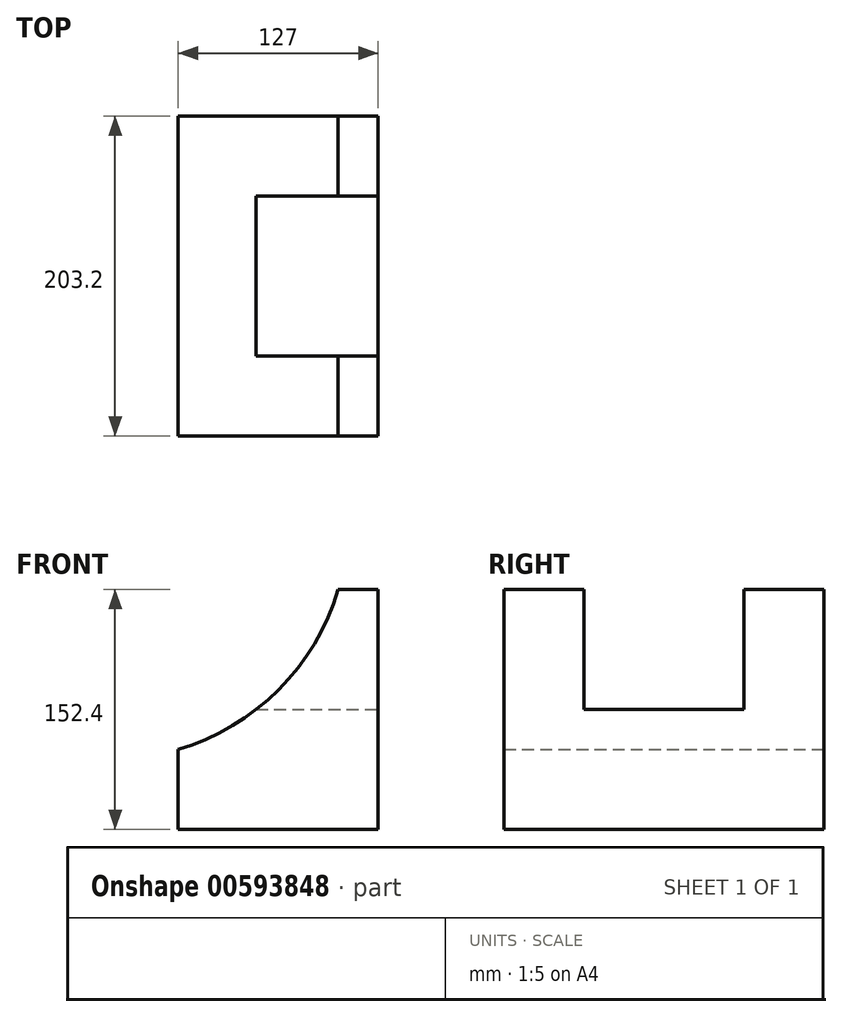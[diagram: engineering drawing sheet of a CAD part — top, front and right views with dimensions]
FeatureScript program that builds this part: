
annotation { "Feature Type Name" : "Feature", "Feature Type Description" : "" }
export const myFeature = defineFeature(function(context is Context, id is Id, definition is map)
    precondition{}
    {
        {
            var Q0;
            Q0=qCreatedBy(makeId("Front.planeOp"),FACE);
            var sketch = newSketch(context, id + "F0", { "sketchPlane" : qUnion([Q0])});
            skLineSegment(sketch, "E0", {"start": v(0, 0) * mm, "end": v(127, 0) * mm});
            skLineSegment(sketch, "E1", {"start": v(127, 0) * mm, "end": v(127, 152.4) * mm});
            skLineSegment(sketch, "E2", {"start": v(127, 152.4) * mm, "end": v(101.6, 152.4) * mm});
            skLineSegment(sketch, "E3", {"start": v(0, 0) * mm, "end": v(0, 50.8) * mm});
            skArc(sketch, "E4", {"start": v(0, 50.8) * mm, "mid": v(63.7, 88.7) * mm, "end": v(101.6, 152.4) * mm});
            skSolve(sketch);
        }
        {
            var Q0;
            Q0 = qSketchRegion(id + "F0", true);
            extrude(context, id + "F1", {"entities" : qUnion([Q0]), "endBound" : BoundingType.SYMMETRIC, "depth" : 203.2 * mm, "offsetDistance" : 25.4 * mm});
        }
        {
            var Q0;
            Q0=makeQuery(id+"F1.opExtrude","SWEPT_FACE",FACE,{"disambiguationData":[OSD([sQuery(id+"F0.wireOp",EDGE,"E1")])]});
            var sketch = newSketch(context, id + "F2", { "sketchPlane" : qUnion([Q0])});
            skLineSegment(sketch, "E5.0", {"start": v(-101.6, 152.4) * mm, "end": v(101.6, 152.4) * mm});
            skPoint(sketch, "E6.0", {"position": v(-101.6, 76.2) * mm});
            skLineSegment(sketch, "E7.0", {"start": v(-101.6, 0) * mm, "end": v(101.6, 0) * mm});
            skLineSegment(sketch, "E8.0", {"start": v(101.6, 0) * mm, "end": v(101.6, 152.4) * mm});
            skLineSegment(sketch, "E9.0.1", {"start": v(101.6, 152.4) * mm, "end": v(-101.6, 152.4) * mm});
            skLineSegment(sketch, "E9.0.2", {"start": v(-101.6, 152.4) * mm, "end": v(-101.6, 0) * mm});
            skLineSegment(sketch, "E10", {"start": v(-50.8, 152.4) * mm, "end": v(-50.8, 76.2) * mm});
            skLineSegment(sketch, "E11", {"start": v(-50.8, 76.2) * mm, "end": v(50.8, 76.2) * mm});
            skLineSegment(sketch, "E12", {"start": v(50.8, 76.2) * mm, "end": v(50.8, 152.4) * mm});
            skSolve(sketch);
        }
        {
            var Q0;
            {var subQ0=sQuery(id+"F2.wireOp",EDGE,"E10");Q0=makeQuery(id+"F2.imprint","IMPRINT",FACE,{"disambiguationData":[TD([[makeQuery(id+"F2.imprint","IMPRINT",EDGE,{"derivedFrom":subQ0}),1.0]])]});}
            extrude(context, id + "F3", {"entities" : qUnion([Q0]), "operationType" : NewBodyOperationType.REMOVE, "endBound" : BoundingType.THROUGH_ALL, "oppositeDirection" : true, "depth" : 25.4 * mm, "offsetDistance" : 25.4 * mm});
        }
    });
